# Revit family: IS_Ceraplan_BD308_BIM_NL
name_source: partatom
category: Plumbing Fixtures
units: mm (PartAtom-declared; Revit-internal decimal feet)

## family parameters
Always vertical = No
Cut with Voids When Loaded = No
OmniClass Number = 23.45.55.17
OmniClass Title = Mixing Faucets
Part Type = Normal
Room Calculation Point = No
Round Connector Dimension = Use Diameter
Shared = No
Work Plane-Based = No

## types (2) — shared parameters
Accesoires = https://www.idealstandard.nl
Accessories = https://www.idealstandard.nl
Afmetingen = 50 x 262 x 170 mm
AfstandsEenheid = Millimeter
Afwerking = Chrom
AreaUnits = millimetres
Artikelnummer = BD308AA
Artikelomschrijving = Ceraplan Einhebel-Küchenmischer Wannenrand mit tief angesetztem Lötauslauf chrom
Artikelreferentie = BD308AA
BIMObjectName = IS_IdealStandard_Sinktaps_Ceraplan_BD308
BIMobject category = Taps & Mixers
BIMobject category code = sanitary-taps-mixers
BIMobject main category = Sanitary
BIMobject main category code = sanitary
BarCode = 3800861107347
Bedieningkraan = einzelne Leber
Beschrijvinggarantie = Herstellergarantie
BimObjectNaam = IS_IdealStandard_Sinktaps_Ceraplan_BD308
Brand = Ideal Standard
Brand url = https://www.idealstandard.nl
Breedte = 50.016409
Category = Taps & Mixer
Color = Chrome
ConnectionType = Plumbing
CurrencyUnit = €
CurrentRevision = 1
Date of publishing = 25/03/2022
Description = Ceraplan Einhebel-Küchenmischer Wannenrand mit tief angesetztem Lötauslauf chrom
Diepte = 262 mm
DurationUnit = Jahre
DuurEenheid = Jahre
Edition number = 1
Eigenschappen = Einhebel-Küchenmischer Wannenrand mit tief angesetztem Lötauslauf chrom
FaucetFunction = Kitchen Mixer
FaucetOperation = Single Lever Kitchen mixer
FaucetTopDescription = Single Lever Kitchen mixer
FaucetType = Kitchen Mixer
Features = Einhebel-Küchenmischer Wannenrand mit tief angesetztem Lötauslauf chrom
Finish = Chrome
Functiekraanwerk = Einhebel-Küchenmischer
GTIN code = https://3800861107347
Garantieonderdelen = 5
Garantieunits = Jahre
GemaaktOp = 25/03/2022
Help = https://www.idealstandard.nl
Hoogte = 170.128444106784
Hulp = https://www.idealstandard.nl
IFC Classification = Sanitary Terminal
IfcExportAs = IfcValveType
IfcExportType = FAUCET
Installatieinstructies = https://www.idealstandard.nl
Installation instructions = https://www.idealstandard.nl
InstallationInstructions = https://www.idealstandard.nl
Klepmechanisme = Einhebel
Kleur = Chrom
Lengte = 262 mm
LinearUnits = millimeters
MainColor = Chrome
MaintenanceInformation = https://www.idealstandard.nl
Manufacturer = Ideal Standard
Manufacturer name = Ideal Standard
ManufacturerURL = https://www.idealstandard.nl
Materiaal = Messing
Material = Messing
Material main = Messing
Merk = Ideal Standard
Model = BD308AA
ModelNumber = BD308AA
ModelReference = Ceraplan Single lever kitchen mixer Rim-Monted with low attached soldered spout chrome
NBS Reference Code = 45-35-70/345
NBS Reference Description = Water supply fittings for sinks
Name = Sinktaps_Ceraplan_BD308_IdealStandard
NettWeight = 1,41 Kg
NominalDepth = 262 mm
NominalHeight = 170 mm
NominalLength = 262 mm
NominalWidth = 50 mm
Normen = Sinktaps_Ceraplan_BD308_IdealStandard
OmniClass Code = 23-31 11 00
OmniClass Description = Faucets
OppervlakteEenheid = Millimeter
Product Guid = f1024d41-02c8-496d-b2a3-6b0dcdc5c57d
Product SKU = BD308
Product certification = https://www.idealstandard.nl
Product data url = https://bimobject.com
Product family = CERAPLAN
Product group = Kitchen Mixers
Product name = Ceraplan Single lever kitchen mixer Rim-Monted with low attached soldered spout chrome
Product url = https://www.idealstandard.nl
ProductInformation = https://www.idealstandard.nl
ProductSoort = Küchenmischer
Productinformatie = https://www.idealstandard.nl
QR code = http://bimobject.com
Revisie = 1
Shape = cylindrical
Size = 50 x 262 x 170 mm
Space = Internal
SpareParts = https://www.idealstandard.nl
Technical description = https://www.idealstandard.nl
Telefoonnummer = 077 355 08 08
Testdruk = 10 bar
Toepassing = Küchenmischer
Typekraanwerk = Einhebel-Küchenmischer
UNSPSC Code = 301815
URL = https://www.idealstandard.nl
Uniclass 1.4 Code = L725111
Uniclass 1.4 Description = Mixer taps
Uniclass 2.0 Code = PR-35-79-79
Uniclass 2.0 Description = Sink Water Supply Fittings
Uniclass 2015 Code = Pr_40_20_87_84
Uniclass 2015 Name = Sink taps
Uniclass2015Beschrijving = Sink taps
Uniclass2015Code = Pr_40_20_87_84
Uniclass2015Referentie = Pr_40_20_87_84
Uniclass2015Title = Sink taps
Uniclass2015Version = v1.25
Uniformat II Code = PR-35-79-79
Uniformat II Description = SinkWaterSupplyFittings
Urlproducent = https://www.idealstandard.nl
ValutaEenheid = Euro
Versie = 1
Version = 1
VolumeUnits = Litres
Volumeunits = Liter
Vorm = zylindrisch
WRASURL = https://www.wrasapprovals.co.uk
WarrantyDescription = manufacturer warranty
WarrantyDurationParts = 5
WarrantyDurationUnit = Years
Wisselstukken = https://www.idealstandard.nl
Youtube clip = https://www.youtube.com
zero-valued in all types: BrutoGewicht, Nettogewicht, Vervangingskosten

## type names (no varying parameters)
- BD308AA - CERAPLAN Single lever kitchen mixer rim- munted with low attached soldered spout chrome - Chrome 1
- BD308AA - CERAPLAN Single lever kitchen mixer rim- munted with low attached soldered spout chrome - Chrome

## geometry (parser evidence)
native form markers: Sweep x2
no freeform markers — native parametric forms only
